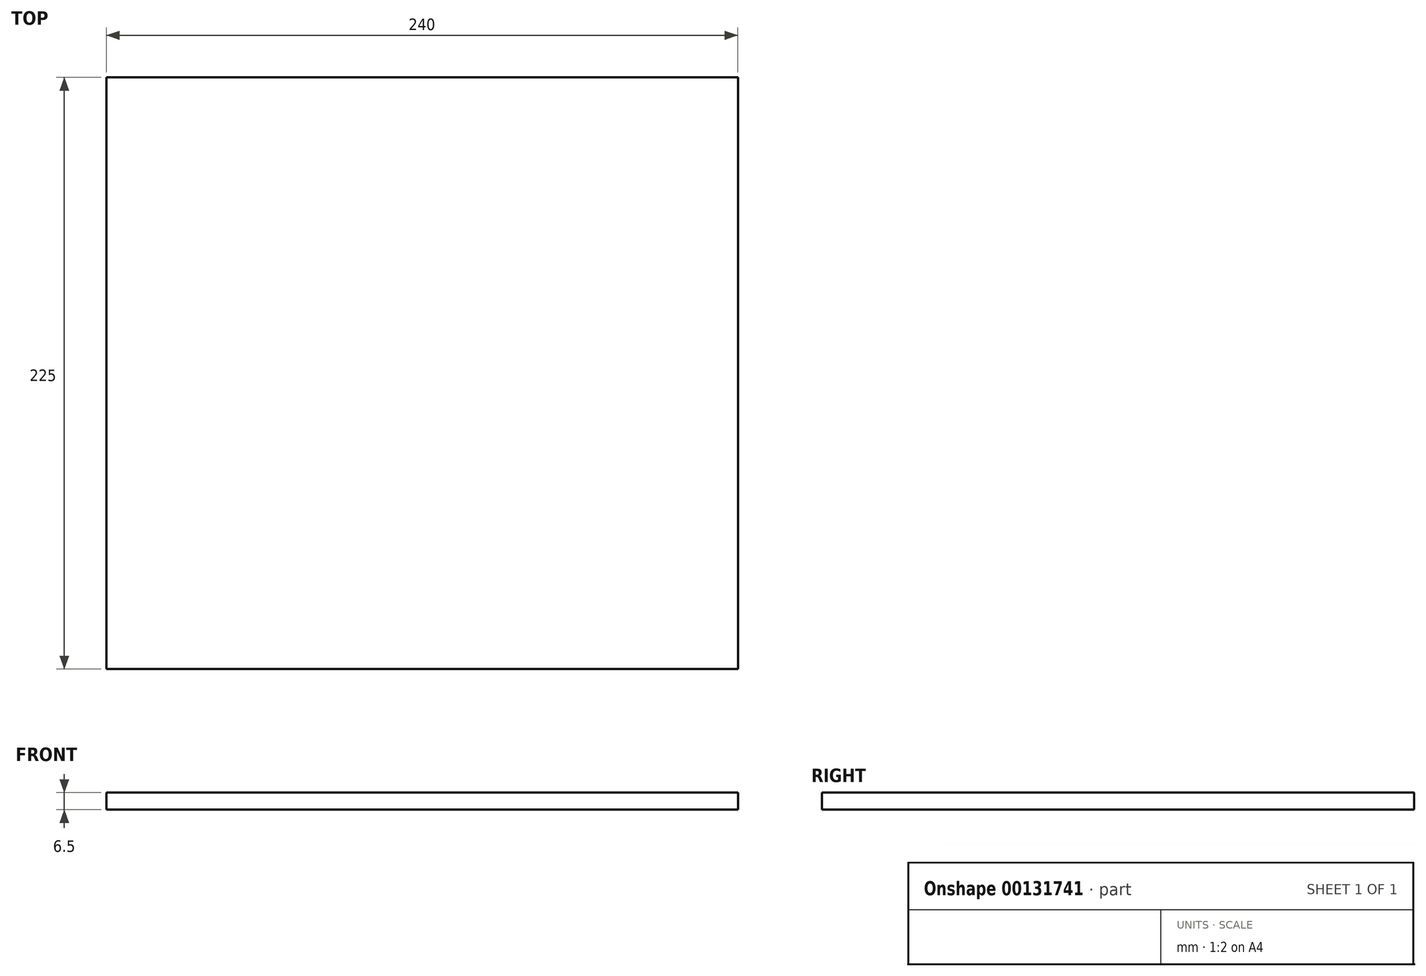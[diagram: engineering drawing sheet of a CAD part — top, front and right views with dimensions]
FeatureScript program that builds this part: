
annotation { "Feature Type Name" : "Feature", "Feature Type Description" : "" }
export const myFeature = defineFeature(function(context is Context, id is Id, definition is map)
    precondition{}
    {
        {
            var Q0;
            Q0=qCreatedBy(makeId("Top.planeOp"),FACE);
            var sketch = newSketch(context, id + "F0", { "sketchPlane" : qUnion([Q0])});
            skLineSegment(sketch, "E0.bottom", {"start": v(-114.8, 136.65) * mm, "end": v(125.2, 136.65) * mm});
            skLineSegment(sketch, "E0.top", {"start": v(-114.8, -88.35) * mm, "end": v(125.2, -88.35) * mm});
            skLineSegment(sketch, "E0.left", {"start": v(-114.8, 136.65) * mm, "end": v(-114.8, -88.35) * mm});
            skLineSegment(sketch, "E0.right", {"start": v(125.2, 136.65) * mm, "end": v(125.2, -88.35) * mm});
            skSolve(sketch);
        }
        {
            var Q0;
            Q0=makeQuery(id+"F0.imprint","IMPRINT",FACE,{"disambiguationData":[TD([[makeQuery(id+"F0.imprint","IMPRINT",EDGE,{"derivedFrom":sQuery(id+"F0.wireOp",EDGE,"E0.bottom")}),-1.0]])]});
            extrude(context, id + "F1", {"entities" : qUnion([Q0]), "depth" : 6.5 * mm});
        }
    });
